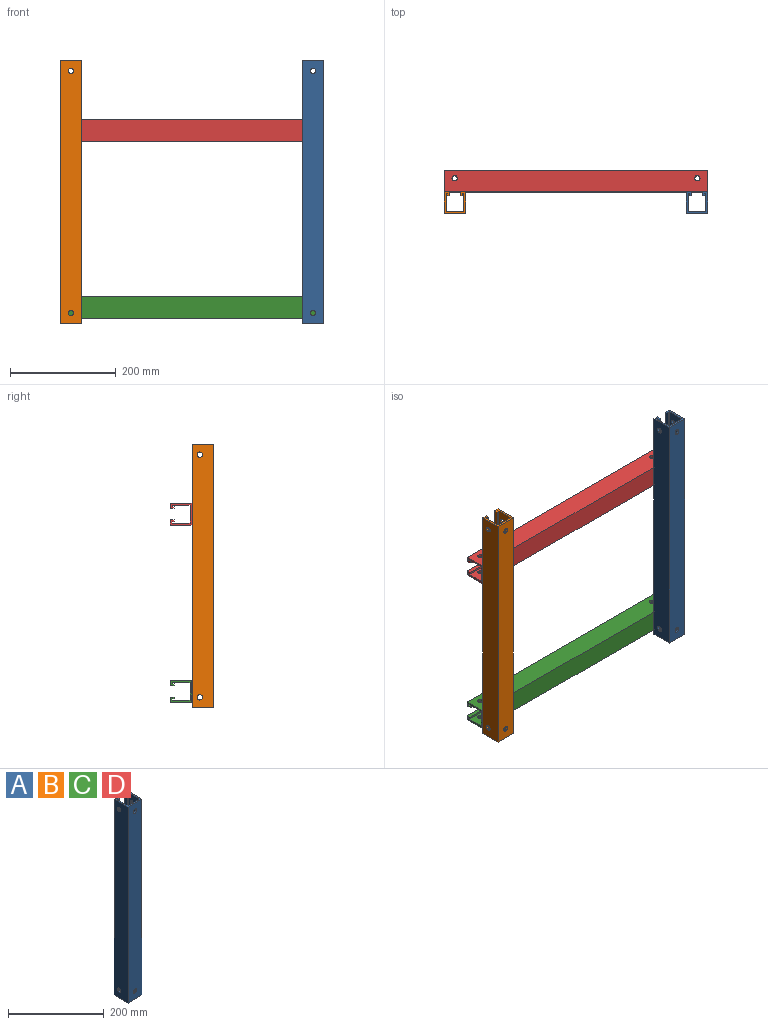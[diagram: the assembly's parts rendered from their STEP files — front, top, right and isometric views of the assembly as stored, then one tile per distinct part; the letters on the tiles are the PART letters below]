
ASSEMBLY  parts=4 mates=8
PART A: 24 faces, bbox 41x41x500 mm
  f0: plane 500x41mm, normal (-1,0,0), area 20342.9mm2, adj f1,f15,f16,f17,f20,f21
  f1: plane 500x41mm, normal (0,-1,0), area 20342.9mm2, adj f0,f2,f16,f17,f18,f19
  f2: plane 500x41mm, normal (1,0,0), area 20342.9mm2, adj f1,f3,f16,f17,f22,f23
  f3: plane 500x9.6mm, normal (0,1,0), area 4800mm2, adj f2,f4,f16,f17
  f4: plane 500x7mm, normal (-1,0,0), area 3500mm2, adj f3,f5,f16,f17
  f5: plane 500x3.4mm, normal (0,-1,0), area 1700mm2, adj f4,f6,f16,f17
  f6: plane 500x3.5mm, normal (1,0,0), area 1750mm2, adj f5,f7,f16,f17
  f7: plane 500x2.5mm, normal (0,-1,0), area 1250mm2, adj f6,f8,f16,f17
  f8: plane 500x33.8mm, normal (-1,0,0), area 16742.9mm2, adj f7,f9,f16,f17,f22,f23
  f9: plane 500x33.6mm, normal (0,1,0), area 16642.9mm2, adj f8,f10,f16,f17,f18,f19
  f10: plane 500x33.8mm, normal (1,0,0), area 16742.9mm2, adj f9,f11,f16,f17,f20,f21
  f11: plane 500x2.5mm, normal (0,-1,0), area 1250mm2, adj f10,f12,f16,f17
  f12: plane 500x3.5mm, normal (-1,0,0), area 1750mm2, adj f11,f13,f16,f17
  f13: plane 500x3.4mm, normal (0,-1,0), area 1700mm2, adj f12,f14,f16,f17
  f14: plane 500x7mm, normal (1,0,0), area 3500mm2, adj f13,f15,f16,f17
  f15: plane 500x9.6mm, normal (0,1,0), area 4800mm2, adj f0,f14,f16,f17
  f16: plane 41x41mm, normal (0,0,1), area 492.8mm2, adj f0,f1,f2,f3,f4,f5,f6,f7
  f17: plane 41x41mm, normal (0,0,-1), area 492.8mm2, adj f0,f1,f2,f3,f4,f5,f6,f7
  f18: cylinder r=5mm len=10mm, axis (0,1,0), area 116.2mm2, adj f1,f9
  f19: cylinder r=5mm len=10mm, axis (0,1,0), area 116.2mm2, adj f1,f9
  f20: cylinder r=5mm len=10mm, axis (-1,0,0), area 116.2mm2, adj f0,f10
  f21: cylinder r=5mm len=10mm, axis (-1,0,0), area 116.2mm2, adj f0,f10
  f22: cylinder r=5mm len=10mm, axis (-1,0,0), area 116.2mm2, adj f2,f8
  f23: cylinder r=5mm len=10mm, axis (-1,0,0), area 116.2mm2, adj f2,f8
PART B: same geometry as A
PART C: same geometry as A
PART D: same geometry as A
PLACE A t=(482.56,-306.37,-73.72)mm
PLACE B t=(23.56,-306.37,-73.72)mm
PLACE C rot(axis=(0,-1,0),90deg) t=(523.56,-265.37,-62.88)mm
PLACE D rot(axis=(0,1,0),90deg) t=(23.56,-265.37,313.88)mm
MATE planar C.f16 <-> B.f0  axis (-1,0,0) through (23.56,-227.87,-25.58)mm
MATE planar B.f15 <-> A.f3  axis (0,1,0) through (28.36,-265.37,176.28)mm
MATE planar B.f16 <-> A.f16  axis (0,0,1) through (64.56,-285.87,426.28)mm
MATE planar C.f17 <-> A.f2  axis (1,0,0) through (523.56,-227.87,-25.58)mm
MATE planar C.f1 <-> B.f15  axis (0,-1,0) through (23.56,-265.37,-42.38)mm
MATE planar D.f1 <-> B.f3  axis (0,-1,0) through (273.56,-265.37,272.88)mm
MATE planar D.f16 <-> A.f2  axis (1,0,0) through (523.56,-227.87,279.08)mm
MATE planar D.f17 <-> B.f0  axis (-1,0,0) through (23.56,-247.26,293.38)mm
